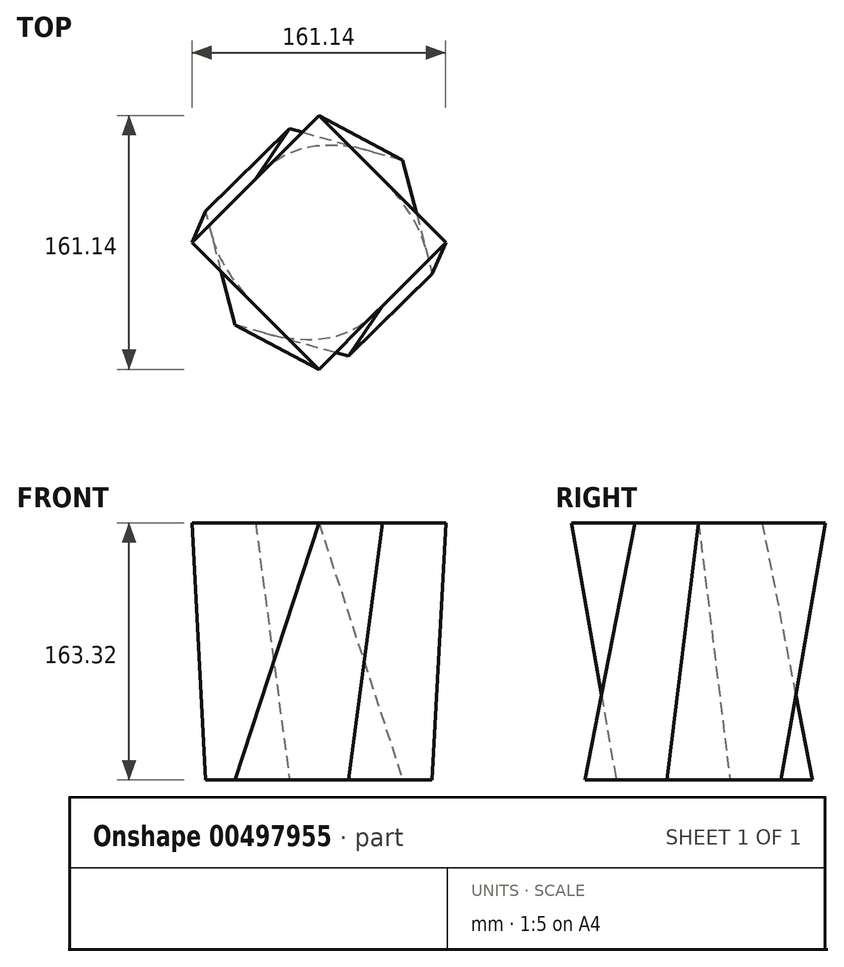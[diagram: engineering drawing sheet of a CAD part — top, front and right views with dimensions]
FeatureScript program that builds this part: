
annotation { "Feature Type Name" : "Feature", "Feature Type Description" : "" }
export const myFeature = defineFeature(function(context is Context, id is Id, definition is map)
    precondition{}
    {
        {
            var Q0;
            Q0=qCreatedBy(makeId("Top.planeOp"),FACE);
            var sketch = newSketch(context, id + "F0", { "sketchPlane" : qUnion([Q0])});
            skCircle(sketch, "E0.cCircle", {"center": v(0, 0) * mm, "radius": 74.66 * mm, "construction": true});
            skLineSegment(sketch, "E0.0", {"start": v(53.25, 52.32) * mm, "end": v(71.94, -19.96) * mm});
            skLineSegment(sketch, "E0.1", {"start": v(71.94, -19.96) * mm, "end": v(18.68, -72.28) * mm});
            skLineSegment(sketch, "E0.2", {"start": v(18.68, -72.28) * mm, "end": v(-53.25, -52.32) * mm});
            skLineSegment(sketch, "E0.3", {"start": v(-53.25, -52.32) * mm, "end": v(-71.94, 19.96) * mm});
            skLineSegment(sketch, "E0.4", {"start": v(-71.94, 19.96) * mm, "end": v(-18.68, 72.28) * mm});
            skLineSegment(sketch, "E0.5", {"start": v(-18.68, 72.28) * mm, "end": v(53.25, 52.32) * mm});
            skSolve(sketch);
        }
        {
            var Q0;
            Q0=qCreatedBy(makeId("Top.planeOp"),FACE);
            cPlane(context, id + "F1", {"entities" : qUnion([Q0]), "cplaneType" : CPlaneType.OFFSET, "offset" : 163.32 * mm, "width" : 152.4 * mm, "height" : 152.4 * mm});
        }
        {
            var Q0;
            Q0=qCreatedBy(id+"F1.planeOp",FACE);
            var sketch = newSketch(context, id + "F2", { "sketchPlane" : qUnion([Q0])});
            skCircle(sketch, "E1.cCircle", {"center": v(0, 0) * mm, "radius": 80.57 * mm, "construction": true});
            skLineSegment(sketch, "E1.0", {"start": v(80.57, 0) * mm, "end": v(0, -80.57) * mm});
            skLineSegment(sketch, "E1.1", {"start": v(0, -80.57) * mm, "end": v(-80.57, 0) * mm});
            skLineSegment(sketch, "E1.2", {"start": v(-80.57, 0) * mm, "end": v(0, 80.57) * mm});
            skLineSegment(sketch, "E1.3", {"start": v(0, 80.57) * mm, "end": v(80.57, 0) * mm});
            skSolve(sketch);
        }
        {
            var Q0;
            Q0=makeQuery(id+"F2.imprint","IMPRINT",FACE,{"disambiguationData":[TD([[makeQuery(id+"F2.imprint","IMPRINT",EDGE,{"derivedFrom":sQuery(id+"F2.wireOp",EDGE,"E1.0")}),-1.0]])]});
            var Q1;
            Q1=makeQuery(id+"F0.imprint","IMPRINT",FACE,{"disambiguationData":[TD([[makeQuery(id+"F0.imprint","IMPRINT",EDGE,{"derivedFrom":sQuery(id+"F0.wireOp",EDGE,"E0.0")}),-1.0]])]});
            loft(context, id + "F3", {"sheetProfilesArray" : [{ "sheetProfileEntities" : qUnion([Q0]) }, { "sheetProfileEntities" : qUnion([Q1]) }]});
        }
    });
